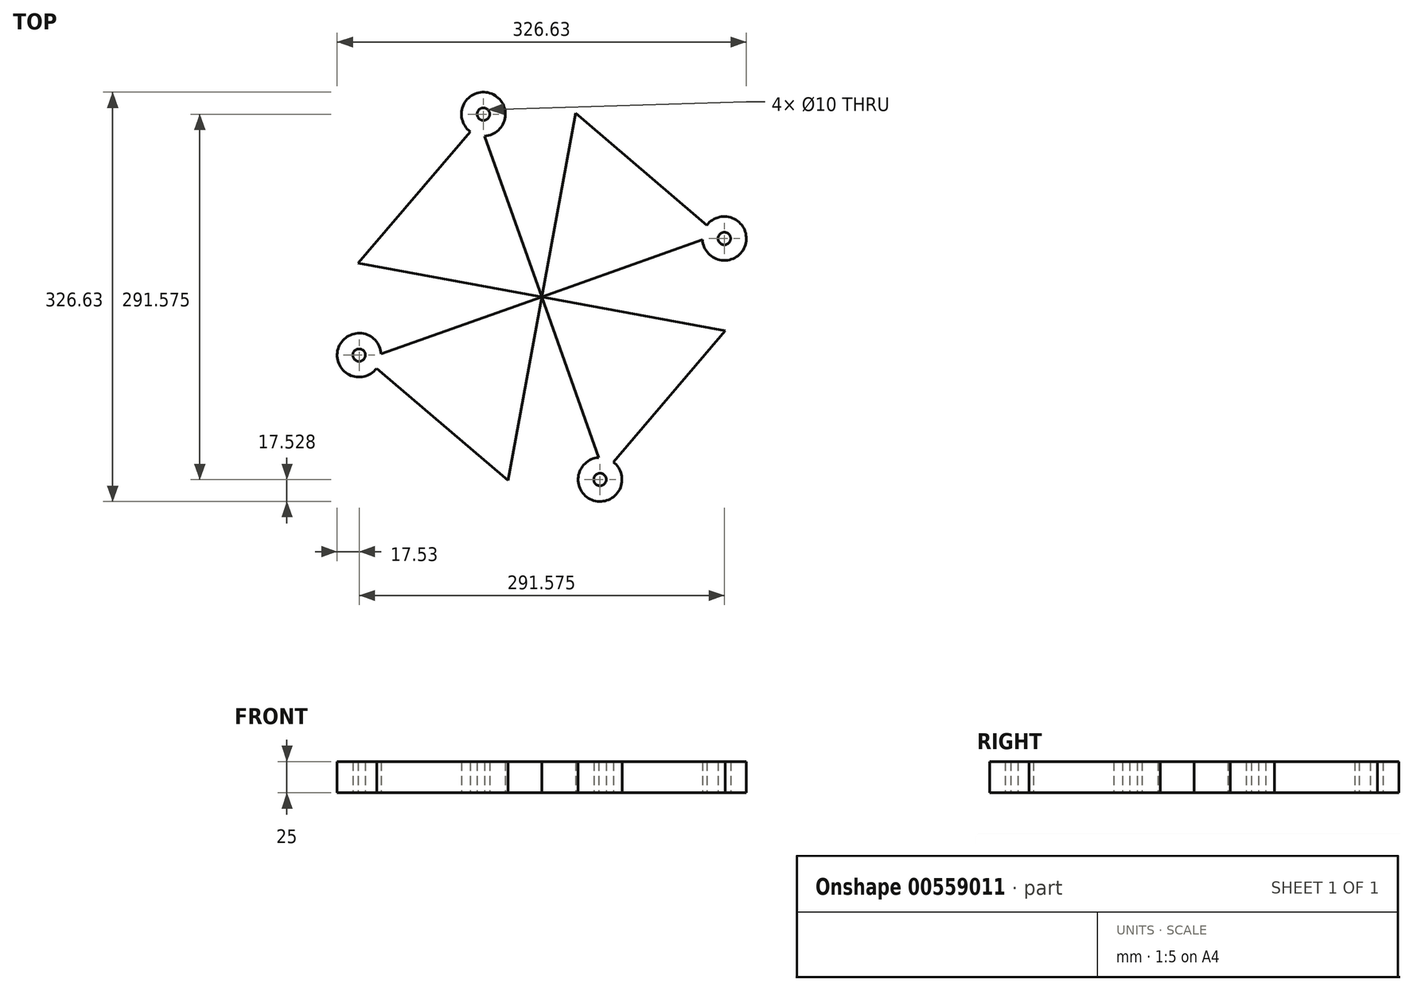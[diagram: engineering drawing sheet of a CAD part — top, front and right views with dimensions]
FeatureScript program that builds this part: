
annotation { "Feature Type Name" : "Feature", "Feature Type Description" : "" }
export const myFeature = defineFeature(function(context is Context, id is Id, definition is map)
    precondition{}
    {
        {
            var Q0;
            Q0=qCreatedBy(makeId("Top.planeOp"),FACE);
            var sketch = newSketch(context, id + "F0", { "sketchPlane" : qUnion([Q0])});
            skCircle(sketch, "E0.cCircle", {"center": v(0, 0) * mm, "radius": 43 * mm, "construction": true});
            skLineSegment(sketch, "E0.0", {"start": v(81.03, 28.77) * mm, "end": v(-15.6, -84.56) * mm});
            skLineSegment(sketch, "E0.1", {"start": v(-15.6, -84.56) * mm, "end": v(-65.43, 55.79) * mm});
            skLineSegment(sketch, "E0.2", {"start": v(-65.43, 55.79) * mm, "end": v(81.03, 28.77) * mm});
            skPoint(sketch, "E0.0.midPoint", {"position": v(32.72, -27.9) * mm});
            skSolve(sketch);
        }
        {
            var Q0;
            Q0=makeQuery(id+"F0.imprint","IMPRINT",FACE,{"disambiguationData":[TD([[makeQuery(id+"F0.imprint","IMPRINT",EDGE,{"derivedFrom":sQuery(id+"F0.wireOp",EDGE,"E0.0")}),-1.0]])]});
            extrude(context, id + "F1", {"entities" : qUnion([Q0]), "depth" : 25 * mm, "offsetDistance" : 25 * mm});
        }
        {
            var Q0;
            Q0=qCreatedBy(makeId("Top.planeOp"),FACE);
            var sketch = newSketch(context, id + "F2", { "sketchPlane" : qUnion([Q0])});
            skCircle(sketch, "E1", {"center": v(-18.89, -90) * mm, "radius": 17.53 * mm});
            skSolve(sketch);
        }
        {
            var Q0;
            Q0 = qSketchRegion(id + "F2", true);
            extrude(context, id + "F3", {"entities" : qUnion([Q0]), "operationType" : NewBodyOperationType.ADD, "depth" : 25 * mm, "offsetDistance" : 25 * mm});
        }
        {
            var Q0;
            Q0=makeQuery(id+"F3.boolean.opBoolean","MERGE",FACE,{"derivedFrom":[makeQuery(id+"F1.opExtrude","CAP_FACE",FACE,{"disambiguationData":[OSD([sQuery(id+"F0.wireOp",EDGE,"E0.0"),sQuery(id+"F0.wireOp",EDGE,"E0.1"),sQuery(id+"F0.wireOp",EDGE,"E0.2")])],"isStart":true}),makeQuery(id+"F3.opExtrude","CAP_FACE",FACE,{"disambiguationData":[OSD([sQuery(id+"F2.wireOp",EDGE,"E1")])],"isStart":true})]});
            var sketch = newSketch(context, id + "F4", { "sketchPlane" : qUnion([Q0])});
            skCircle(sketch, "E2", {"center": v(-18.89, 90) * mm, "radius": 7.32 * mm});
            skSolve(sketch);
        }
        {
            var Q0;
            Q0=sQuery(id+"F4.wireOp",VERTEX,"E2.center");
            var Q1;
            Q1=makeQuery(id+"F1.opExtrude","SWEPT_BODY",BODY,{"disambiguationData":[OSD([sQuery(id+"F0.wireOp",EDGE,"E0.0"),sQuery(id+"F0.wireOp",EDGE,"E0.1"),sQuery(id+"F0.wireOp",EDGE,"E0.2")])]});
            hole(context, id + "F5", {"style" : HoleStyle.SIMPLE, "endStyle" : HoleEndStyle.THROUGH, "holeDiameter" : 10 * mm, "isTappedThrough" : true, "tappedDepth" : 12 * mm, "tapClearance" : 3, "locations" : qUnion([Q0]), "scope" : qUnion([Q1])});
        }
        {
            var Q0;
            Q0=makeQuery(id+"F1.opExtrude","SWEPT_BODY",BODY,{"disambiguationData":[OSD([sQuery(id+"F0.wireOp",EDGE,"E0.0"),sQuery(id+"F0.wireOp",EDGE,"E0.1"),sQuery(id+"F0.wireOp",EDGE,"E0.2")])]});
            var Q1;
            Q1=makeQuery(id+"F1.opExtrude","SWEPT_EDGE",EDGE,{"disambiguationData":[OSD([sQuery(id+"F0.wireOp",EDGE,"E0.1"),sQuery(id+"F0.wireOp",EDGE,"E0.2")])]});
            circularPattern(context, id + "F6", {"entities" : qUnion([Q0]), "axis" : qUnion([Q1]), "angle" : 360 * degree, "instanceCount" : 4, "equalSpace" : true});
        }
    });
